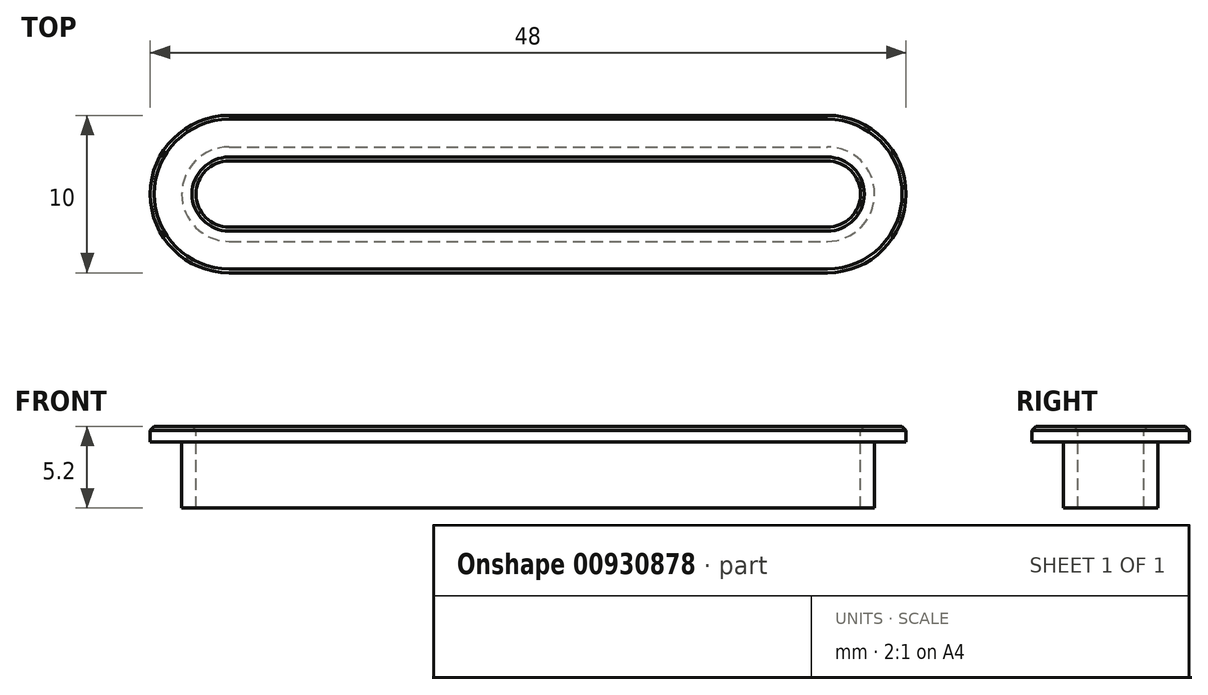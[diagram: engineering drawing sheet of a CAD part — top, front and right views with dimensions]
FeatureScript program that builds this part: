
annotation { "Feature Type Name" : "Feature", "Feature Type Description" : "" }
export const myFeature = defineFeature(function(context is Context, id is Id, definition is map)
    precondition{}
    {
        {
            var Q0;
            Q0=qCreatedBy(makeId("Top.planeOp"),FACE);
            var sketch = newSketch(context, id + "F0", { "sketchPlane" : qUnion([Q0])});
            skArc(sketch, "E0", {"start": v(-19, 3) * mm, "mid": v(-22, 0) * mm, "end": v(-19, -3) * mm});
            skArc(sketch, "E1", {"start": v(19, -3) * mm, "mid": v(22, 0) * mm, "end": v(19, 3) * mm});
            skLineSegment(sketch, "E2", {"start": v(-19, 3) * mm, "end": v(19, 3) * mm});
            skLineSegment(sketch, "E3", {"start": v(-19, -3) * mm, "end": v(19, -3) * mm});
            skLineSegment(sketch, "E4", {"start": v(-19, 3) * mm, "end": v(19, -3) * mm, "construction": true});
            skSolve(sketch);
        }
        {
            var Q0;
            Q0 = qSketchRegion(id + "F0", true);
            extrude(context, id + "F1", {"entities" : qUnion([Q0]), "oppositeDirection" : true, "depth" : 4.2 * mm, "offsetDistance" : 25 * mm});
        }
        {
            var Q0;
            Q0=makeQuery(id+"F1.opExtrude","CAP_FACE",FACE,{"disambiguationData":[OSD([sQuery(id+"F0.wireOp",EDGE,"E0"),sQuery(id+"F0.wireOp",EDGE,"E1"),sQuery(id+"F0.wireOp",EDGE,"E2"),sQuery(id+"F0.wireOp",EDGE,"E3")])],"isStart":true});
            var sketch = newSketch(context, id + "F2", { "sketchPlane" : qUnion([Q0])});
            skLineSegment(sketch, "E5.0", {"start": v(-19, -5) * mm, "end": v(19, -5) * mm});
            skArc(sketch, "E5.1", {"start": v(-19, 5) * mm, "mid": v(-24, 0) * mm, "end": v(-19, -5) * mm});
            skLineSegment(sketch, "E5.2", {"start": v(19, 5) * mm, "end": v(-19, 5) * mm});
            skArc(sketch, "E5.3", {"start": v(19, -5) * mm, "mid": v(24, 0) * mm, "end": v(19, 5) * mm});
            skSolve(sketch);
        }
        {
            var Q0;
            Q0 = qSketchRegion(id + "F2", true);
            extrude(context, id + "F3", {"entities" : qUnion([Q0]), "operationType" : NewBodyOperationType.ADD, "depth" : 1 * mm, "offsetDistance" : 25 * mm});
        }
        {
            var Q0;
            Q0=makeQuery(id+"F3.opExtrude","CAP_FACE",FACE,{"disambiguationData":[OSD([sQuery(id+"F2.wireOp",EDGE,"E5.0"),sQuery(id+"F2.wireOp",EDGE,"E5.1"),sQuery(id+"F2.wireOp",EDGE,"E5.2"),sQuery(id+"F2.wireOp",EDGE,"E5.3")])],"isStart":false});
            var sketch = newSketch(context, id + "F4", { "sketchPlane" : qUnion([Q0])});
            skArc(sketch, "E6", {"start": v(19, -2.1) * mm, "mid": v(21.1, 0) * mm, "end": v(19, 2.1) * mm});
            skArc(sketch, "E7", {"start": v(-19, 2.1) * mm, "mid": v(-21.1, 0) * mm, "end": v(-19, -2.1) * mm});
            skLineSegment(sketch, "E8", {"start": v(-19, 2.1) * mm, "end": v(19, 2.1) * mm});
            skLineSegment(sketch, "E9", {"start": v(-19, -2.1) * mm, "end": v(19, -2.1) * mm});
            skSolve(sketch);
        }
        {
            var Q0;
            Q0 = qSketchRegion(id + "F4", true);
            extrude(context, id + "F5", {"entities" : qUnion([Q0]), "operationType" : NewBodyOperationType.REMOVE, "endBound" : BoundingType.THROUGH_ALL, "oppositeDirection" : true, "depth" : 25 * mm, "offsetDistance" : 25 * mm});
        }
        {
            var Q0;
            Q0=makeQuery(id+"F3.opExtrude","CAP_FACE",FACE,{"disambiguationData":[OSD([sQuery(id+"F2.wireOp",EDGE,"E5.0"),sQuery(id+"F2.wireOp",EDGE,"E5.1"),sQuery(id+"F2.wireOp",EDGE,"E5.2"),sQuery(id+"F2.wireOp",EDGE,"E5.3")])],"isStart":false});
            chamfer(context, id + "F6", {"entities" : qUnion([Q0]), "width" : 0.25 * mm, "tangentPropagation" : true});
        }
    });
